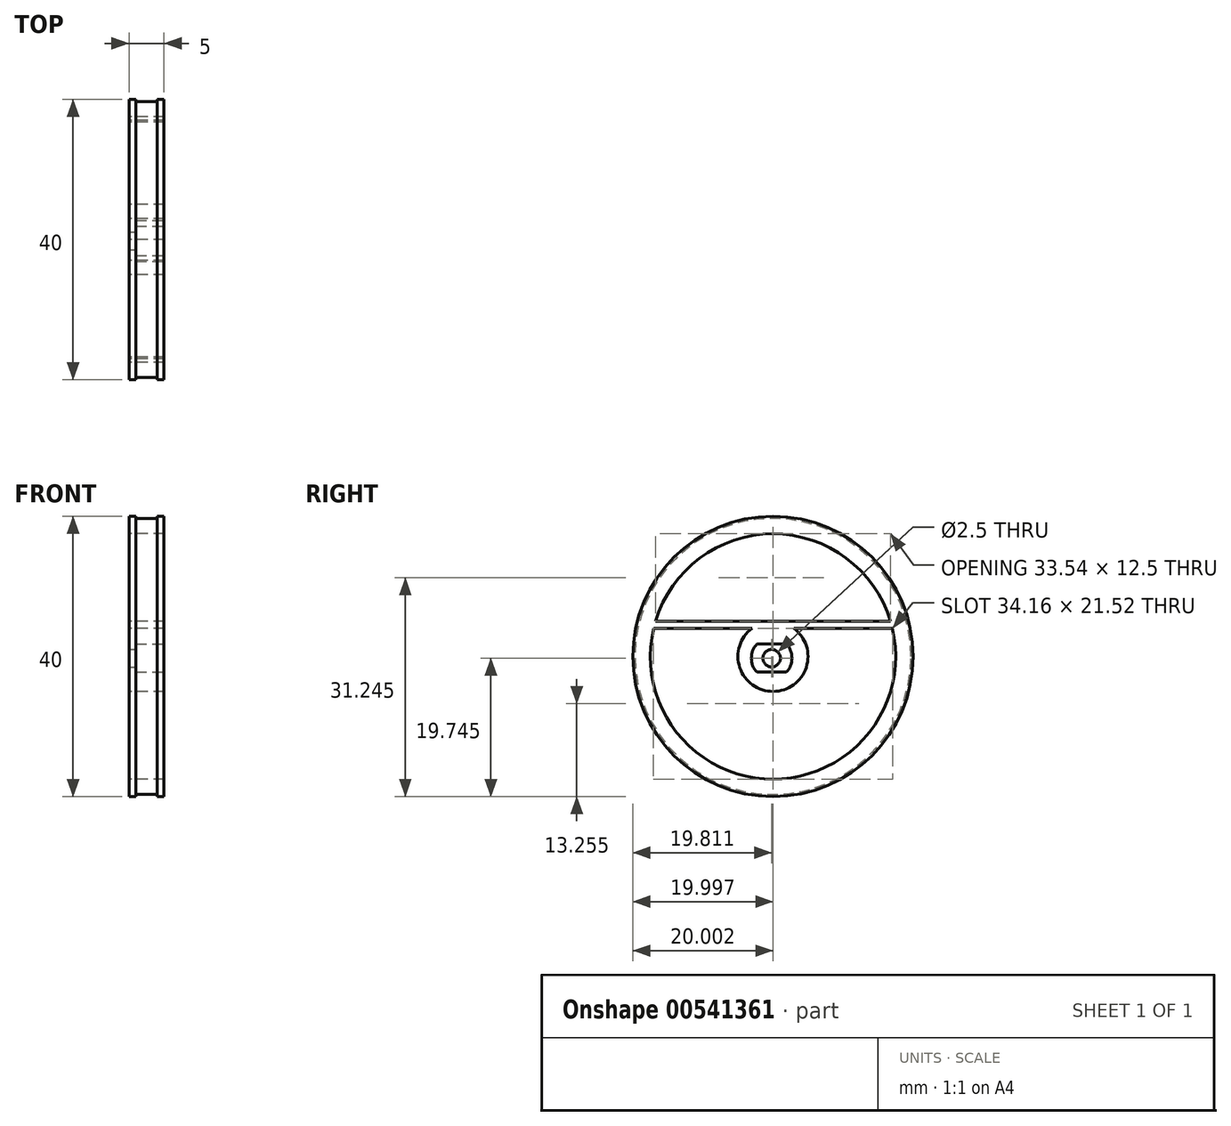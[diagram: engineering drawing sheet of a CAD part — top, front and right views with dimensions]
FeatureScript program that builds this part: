
annotation { "Feature Type Name" : "Feature", "Feature Type Description" : "" }
export const myFeature = defineFeature(function(context is Context, id is Id, definition is map)
    precondition{}
    {
        {
            var Q0;
            Q0=qCreatedBy(makeId("Front.planeOp"),FACE);
            var sketch = newSketch(context, id + "F0", { "sketchPlane" : qUnion([Q0])});
            skLineSegment(sketch, "E0.bottom", {"start": v(0, 43.37) * mm, "end": v(1, 43.37) * mm});
            skLineSegment(sketch, "E0.top", {"start": v(0, 40.87) * mm, "end": v(5, 40.87) * mm});
            skLineSegment(sketch, "E0.left", {"start": v(0, 43.37) * mm, "end": v(0, 40.87) * mm});
            skLineSegment(sketch, "E0.right", {"start": v(5, 43.37) * mm, "end": v(5, 40.87) * mm});
            skLineSegment(sketch, "E1.top", {"start": v(4, 43.07) * mm, "end": v(1, 43.07) * mm});
            skLineSegment(sketch, "E1.left", {"start": v(4, 43.37) * mm, "end": v(4, 43.07) * mm});
            skLineSegment(sketch, "E1.right", {"start": v(1, 43.37) * mm, "end": v(1, 43.07) * mm});
            skLineSegment(sketch, "E2.trimOffspring", {"start": v(4, 43.37) * mm, "end": v(5, 43.37) * mm});
            skLineSegment(sketch, "E3.bottom", {"start": v(0, 28.37) * mm, "end": v(5, 28.37) * mm});
            skLineSegment(sketch, "E3.top", {"start": v(0, 23.37) * mm, "end": v(5, 23.37) * mm});
            skLineSegment(sketch, "E3.left", {"start": v(0, 28.37) * mm, "end": v(0, 23.37) * mm});
            skLineSegment(sketch, "E3.right", {"start": v(5, 28.37) * mm, "end": v(5, 23.37) * mm});
            skSolve(sketch);
        }
        {
            var Q0;
            Q0=makeQuery(id+"F0.imprint","IMPRINT",FACE,{"disambiguationData":[TD([[makeQuery(id+"F0.imprint","IMPRINT",EDGE,{"derivedFrom":sQuery(id+"F0.wireOp",EDGE,"E3.bottom")}),-1.0]])]});
            var Q1;
            Q1=makeQuery(id+"F0.imprint","IMPRINT",FACE,{"disambiguationData":[TD([[makeQuery(id+"F0.imprint","IMPRINT",EDGE,{"derivedFrom":sQuery(id+"F0.wireOp",EDGE,"E0.bottom")}),-1.0]])]});
            var Q2;
            Q2=sQuery(id+"F0.wireOp",EDGE,"E3.top");
            revolve(context, id + "F1", {"entities" : qUnion([Q0, Q1]), "axis" : qUnion([Q2]), "revolveType" : RevolveType.FULL});
        }
        {
            var Q0;
            Q0=qCreatedBy(makeId("Right.planeOp"),FACE);
            var sketch = newSketch(context, id + "F2", { "sketchPlane" : qUnion([Q0])});
            skLineSegment(sketch, "E4.bottom", {"start": v(0, 28.38) * mm, "end": v(16.76, 28.38) * mm});
            skLineSegment(sketch, "E4.top", {"start": v(2.98, 27.38) * mm, "end": v(17.03, 27.38) * mm});
            skLineSegment(sketch, "E4.left", {"start": v(0, 28.38) * mm, "end": v(0, 28.37) * mm});
            skArc(sketch, "E5.0", {"start": v(2.98, 27.38) * mm, "mid": v(1.57, 28.11) * mm, "end": v(0, 28.37) * mm});
            skLineSegment(sketch, "E6", {"start": v(16.9, 27.88) * mm, "end": v(2.14, 27.88) * mm, "construction": true});
            skLineSegment(sketch, "E7", {"start": v(17.03, 27.38) * mm, "end": v(17.81, 27.38) * mm});
            skLineSegment(sketch, "E8", {"start": v(17.81, 27.38) * mm, "end": v(17.81, 28.38) * mm});
            skLineSegment(sketch, "E9", {"start": v(17.81, 28.38) * mm, "end": v(16.76, 28.38) * mm});
            skSolve(sketch);
        }
        {
            var Q0;
            Q0 = qSketchRegion(id + "F2", true);
            var Q1;
            Q1=makeQuery(id+"F1.opRevolve","SWEPT_FACE",FACE,{"disambiguationData":[OSD([sQuery(id+"F0.wireOp",EDGE,"E0.right")])]});
            extrude(context, id + "F3", {"entities" : qUnion([Q0]), "operationType" : NewBodyOperationType.ADD, "endBound" : BoundingType.UP_TO_SURFACE, "depth" : 1 * mm, "endBoundEntityFace" : qUnion([Q1]), "offsetDistance" : 25 * mm});
        }
        {
            var Q0;
            Q0=makeQuery(id+"F1.opRevolve","SWEPT_FACE",FACE,{"disambiguationData":[OSD([sQuery(id+"F0.wireOp",EDGE,"E3.right")])]});
            var sketch = newSketch(context, id + "F4", { "sketchPlane" : qUnion([Q0])});
            skArc(sketch, "E10", {"start": v(-2.29, 25.12) * mm, "mid": v(-3.09, 23.12) * mm, "end": v(-2.29, 21.12) * mm});
            skCircle(sketch, "E11.0", {"center": v(-0.19, 23.12) * mm, "radius": 5 * mm, "construction": true});
            skLineSegment(sketch, "E12", {"start": v(-2.29, 25.12) * mm, "end": v(1.91, 25.12) * mm});
            skLineSegment(sketch, "E13", {"start": v(-2.29, 21.12) * mm, "end": v(1.91, 21.12) * mm});
            skArc(sketch, "E14.trimOffspring", {"start": v(1.91, 21.12) * mm, "mid": v(2.71, 23.12) * mm, "end": v(1.91, 25.12) * mm});
            skSolve(sketch);
        }
        {
            var Q0;
            Q0=makeQuery(id+"F4.imprint","IMPRINT",FACE,{"disambiguationData":[TD([[makeQuery(id+"F4.imprint","IMPRINT",EDGE,{"derivedFrom":sQuery(id+"F4.wireOp",EDGE,"E10")}),1.0]])]});
            extrude(context, id + "F5", {"entities" : qUnion([Q0]), "operationType" : NewBodyOperationType.REMOVE, "oppositeDirection" : true, "depth" : 4 * mm, "offsetDistance" : 25 * mm});
        }
        {
            var Q0;
            Q0=makeQuery(id+"F5.boolean.opBoolean","COPY",FACE,{"derivedFrom":makeQuery(id+"F5.opExtrude","CAP_FACE",FACE,{"disambiguationData":[OSD([sQuery(id+"F4.wireOp",EDGE,"E10"),sQuery(id+"F4.wireOp",EDGE,"E12"),sQuery(id+"F4.wireOp",EDGE,"E13"),sQuery(id+"F4.wireOp",EDGE,"E14.trimOffspring")])],"isStart":false})});
            var sketch = newSketch(context, id + "F6", { "sketchPlane" : qUnion([Q0])});
            skCircle(sketch, "E15", {"center": v(-0.19, 23.12) * mm, "radius": 1.25 * mm});
            skArc(sketch, "E16.0", {"start": v(-2.29, 25.12) * mm, "mid": v(-3.09, 23.12) * mm, "end": v(-2.29, 21.12) * mm, "construction": true});
            skSolve(sketch);
        }
        {
            var Q0;
            Q0 = qSketchRegion(id + "F6", true);
            extrude(context, id + "F7", {"entities" : qUnion([Q0]), "operationType" : NewBodyOperationType.REMOVE, "endBound" : BoundingType.UP_TO_NEXT, "oppositeDirection" : true, "depth" : 25 * mm, "offsetDistance" : 25 * mm});
        }
        {
            var Q0;
            Q0=qCreatedBy(makeId("Right.planeOp"),FACE);
            var sketch = newSketch(context, id + "F8", { "sketchPlane" : qUnion([Q0])});
            skCircle(sketch, "E17.0", {"center": v(0, 23.37) * mm, "radius": 5 * mm, "construction": true});
            skLineSegment(sketch, "E18.bottom", {"start": v(0, 28.37) * mm, "end": v(-18.63, 28.37) * mm});
            skLineSegment(sketch, "E18.top", {"start": v(0, 27.37) * mm, "end": v(-18.63, 27.37) * mm});
            skLineSegment(sketch, "E18.left", {"start": v(0, 28.37) * mm, "end": v(0, 27.37) * mm});
            skLineSegment(sketch, "E18.right", {"start": v(-18.63, 28.37) * mm, "end": v(-18.63, 27.37) * mm});
            skSolve(sketch);
        }
        {
            var Q0;
            Q0=makeQuery(id+"F8.imprint","IMPRINT",FACE,{"disambiguationData":[TD([[makeQuery(id+"F8.imprint","IMPRINT",EDGE,{"derivedFrom":sQuery(id+"F8.wireOp",EDGE,"E18.bottom")}),1.0]])]});
            var Q1;
            {var subQ0=sQuery(id+"F0.wireOp",EDGE,"E3.right");var subQ1=sQuery(id+"F0.wireOp",EDGE,"E0.right");Q1=makeQuery(id+"F5CIg5ViPLkcpVU_1.1.F8NBmociQbi9ti4_1.6.F3.boolean.opBoolean","MERGE",FACE,{"derivedFrom":[makeQuery(id+"F5CIg5ViPLkcpVU_1.1.F8NBmociQbi9ti4_1.5.F3.boolean.opBoolean","MERGE",FACE,{"derivedFrom":[makeQuery(id+"F5CIg5ViPLkcpVU_1.1.F8NBmociQbi9ti4_1.4.F3.boolean.opBoolean","MERGE",FACE,{"derivedFrom":[makeQuery(id+"F5CIg5ViPLkcpVU_1.1.F8NBmociQbi9ti4_1.3.F3.boolean.opBoolean","MERGE",FACE,{"derivedFrom":[makeQuery(id+"F5CIg5ViPLkcpVU_1.1.F8NBmociQbi9ti4_1.2.F3.boolean.opBoolean","MERGE",FACE,{"derivedFrom":[makeQuery(id+"F5CIg5ViPLkcpVU_1.1.F8NBmociQbi9ti4_1.1.F3.boolean.opBoolean","MERGE",FACE,{"derivedFrom":[makeQuery(id+"F8NBmociQbi9ti4_1.7.F3.boolean.opBoolean","MERGE",FACE,{"derivedFrom":[makeQuery(id+"F8NBmociQbi9ti4_1.6.F3.boolean.opBoolean","MERGE",FACE,{"derivedFrom":[makeQuery(id+"F8NBmociQbi9ti4_1.5.F3.boolean.opBoolean","MERGE",FACE,{"derivedFrom":[makeQuery(id+"F8NBmociQbi9ti4_1.4.F3.boolean.opBoolean","MERGE",FACE,{"derivedFrom":[makeQuery(id+"F8NBmociQbi9ti4_1.3.F3.boolean.opBoolean","MERGE",FACE,{"derivedFrom":[makeQuery(id+"F8NBmociQbi9ti4_1.2.F3.boolean.opBoolean","MERGE",FACE,{"derivedFrom":[makeQuery(id+"F8NBmociQbi9ti4_1.1.F3.boolean.opBoolean","MERGE",FACE,{"derivedFrom":[makeQuery(id+"F3.boolean.opBoolean","MERGE",FACE,{"derivedFrom":[makeQuery(id+"F1.opRevolve","SWEPT_FACE",FACE,{"disambiguationData":[OSD([subQ1])]}),makeQuery(id+"F1.opRevolve","SWEPT_FACE",FACE,{"disambiguationData":[OSD([subQ0])]}),makeQuery(id+"F3.opExtrude","CAP_FACE",FACE,{"disambiguationData":[OSD([subQ1])],"isStart":false})]}),makeQuery(id+"F8NBmociQbi9ti4_1.1.F3.opExtrude","CAP_FACE",FACE,{"disambiguationData":[OSD([subQ1,subQ0])],"isStart":false})]}),makeQuery(id+"F8NBmociQbi9ti4_1.2.F3.opExtrude","CAP_FACE",FACE,{"disambiguationData":[OSD([subQ1,subQ0])],"isStart":false})]}),makeQuery(id+"F8NBmociQbi9ti4_1.3.F3.opExtrude","CAP_FACE",FACE,{"disambiguationData":[OSD([subQ1,subQ0])],"isStart":false})]}),makeQuery(id+"F8NBmociQbi9ti4_1.4.F3.opExtrude","CAP_FACE",FACE,{"disambiguationData":[OSD([subQ1,subQ0])],"isStart":false})]}),makeQuery(id+"F8NBmociQbi9ti4_1.5.F3.opExtrude","CAP_FACE",FACE,{"disambiguationData":[OSD([subQ1,subQ0])],"isStart":false})]}),makeQuery(id+"F8NBmociQbi9ti4_1.6.F3.opExtrude","CAP_FACE",FACE,{"disambiguationData":[OSD([subQ1,subQ0])],"isStart":false})]}),makeQuery(id+"F8NBmociQbi9ti4_1.7.F3.opExtrude","CAP_FACE",FACE,{"disambiguationData":[OSD([subQ1,subQ0])],"isStart":false})]}),makeQuery(id+"F5CIg5ViPLkcpVU_1.1.F8NBmociQbi9ti4_1.1.F3.opExtrude","CAP_FACE",FACE,{"disambiguationData":[OSD([subQ1,subQ0])],"isStart":false})]}),makeQuery(id+"F5CIg5ViPLkcpVU_1.1.F8NBmociQbi9ti4_1.2.F3.opExtrude","CAP_FACE",FACE,{"disambiguationData":[OSD([subQ1,subQ0])],"isStart":false})]}),makeQuery(id+"F5CIg5ViPLkcpVU_1.1.F8NBmociQbi9ti4_1.3.F3.opExtrude","CAP_FACE",FACE,{"disambiguationData":[OSD([subQ1,subQ0])],"isStart":false})]}),makeQuery(id+"F5CIg5ViPLkcpVU_1.1.F8NBmociQbi9ti4_1.4.F3.opExtrude","CAP_FACE",FACE,{"disambiguationData":[OSD([subQ1,subQ0])],"isStart":false})]}),makeQuery(id+"F5CIg5ViPLkcpVU_1.1.F8NBmociQbi9ti4_1.5.F3.opExtrude","CAP_FACE",FACE,{"disambiguationData":[OSD([subQ1,subQ0])],"isStart":false})]}),makeQuery(id+"F5CIg5ViPLkcpVU_1.1.F8NBmociQbi9ti4_1.6.F3.opExtrude","CAP_FACE",FACE,{"disambiguationData":[OSD([subQ1,subQ0])],"isStart":false})]});}
            extrude(context, id + "F9", {"entities" : qUnion([Q0]), "operationType" : NewBodyOperationType.ADD, "endBound" : BoundingType.UP_TO_SURFACE, "depth" : 1 * mm, "endBoundEntityFace" : qUnion([Q1]), "offsetDistance" : 25 * mm});
        }
    });
